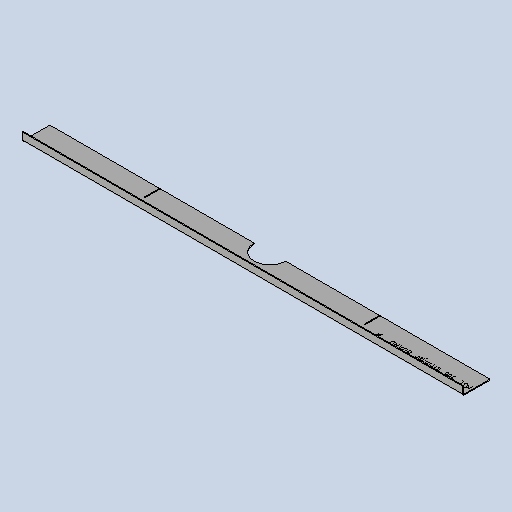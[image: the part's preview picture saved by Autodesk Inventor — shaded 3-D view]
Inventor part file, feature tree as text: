
AUTODESK INVENTOR PART (.ipt)
format: ipt  version: 2025 (Build 290162010, 162A)  size: 275,456 bytes
history: native  units: mm
features: other x5, sheet_metal_op x4, sketch x4, extrude x1
ambient origin geometry x8: Origin, YZ Plane, XZ Plane, XY Plane, X Axis, Y Axis, Z Axis, Center Point
bodies: Solid1 (feature_tree)
feature tree (14):
  sheet_metal_op  "Face1"
  sheet_metal_op  "Flange1"
  extrude  "Extrusion1"  Depth=62.0mm
  other  "Mark2"
  other  "A-Side Definition"
  sketch  "Sketch1"  dims[d0=980.0mm d1=62.0mm]
  other  "Plate1"
  sketch  "Sketch2"  dims[d2=2.0mm]
  other  "Plate2"
  sheet_metal_op  "Bend1"
  sheet_metal_op  "Corner1"
  sketch  "Sketch5"  dims[d3=2.0mm]
  sketch  "Sketch9"  dims[d4=1.0mm d5=4.0mm d6=2.75mm d7=20.0mm d8=90.0deg d9=2.75mm d10=8.0mm d11=2.0mm d12=2.75mm d15=0.0mm d16=0.0mm d40=200.0mm d41=12.0mm d45=70.0mm d48=2.1mm d49=490.0mm d51=29.0mm d52=33.0mm]
  other  "Definition1"
